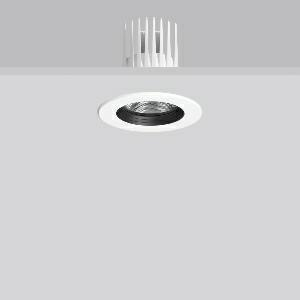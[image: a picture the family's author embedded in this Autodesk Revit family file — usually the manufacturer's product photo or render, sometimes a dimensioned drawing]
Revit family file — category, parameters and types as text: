
# Revit family: heledon_mini_e_901750_002_3_76_2cef
name_source: partatom
category: Lighting Fixtures
units: mm (PartAtom-declared; Revit-internal decimal feet)

## family parameters
Cut with Voids When Loaded = No
Host = Face
Light Source = No
Part Type = Normal
Room Calculation Point = No
Round Connector Dimension = Use Diameter
Shared = No

## types (1)
- HELEDON mini E (1 x LED Modul 935, 3800 lm, 3500)
    Apparent Load = 29 VA
    Approval mark = CE
    CIE Flux Codes = 95 99 100 100 100
    Color Rendering = 92
    Color Temperature = 3500
    Default Elevation = 1800 mm
    Description = Series: HELEDON mini
Round recessed downlight. Housing: die-cast aluminium, powder-coated. Black plastic ring and recessed LED to prevent glare from the side. Optical assembly with reflector made of MIRO-Silver with 98% total light reflection for outstanding efficiency - can be changed without tools. Best colour rendering index Ra>90. Suitable for Recessed ceiling mounting. Installation without tools thanks to spring fastening system. Including separate LED converter with connecting cable 600 mm.High quality converter without flickering and stroboscopic effect. Through-wiring box (5 pole) available as accessory. The following accessories can be mounted without use of tools: interchangeable lenses, decorative glasses, honeycomb louvre, clear and frosted diffusers, white interchangeable plastic ring. 
Colour: traffic white, matt (RAL 9016)
Diameter: 124 mm
Height: 3 mm
Cut-out diameter: 114 mm
Recess height: 170 mm
Luminaire: recess height: 120 mm
Lamp: LED
Socket: without socket
Colour temperature: 3500K
Colour rendering index (CRI): 92
System power: 29 W
Rated luminous flux: 3800 lm
Luminous efficiency: 131 lm/W
Control gear: Converter, dimmable, DALI
Protection class: II
Type of protection: IP 20
    Height = 0 mm  [stored 0 ft]
    Lamp = 1 x LED Modul 935
    Lamp Light Flux = 3800 lm
    Lamp count = 1
    Length = 124 mm  [stored 0.406824 ft]
    Lifetime = 50000 h
    Luminous efficacy = 131 lm/W
    Manufacturer = RZB
    ModVariant = No
    Model = 901750.002.3.76
    Mounting Place = Ceiling
    Mounting Type = Recessed
    Number of Poles = 1
    OnlyDefault = Yes
    Power Factor = 1
    Product Name = HELEDON mini E
    Product group = Recessed downlights
    ProductGroupID = 402
    Protection Class = Protection class II
    Protection Degree = IP 20
    RLX_Detail_Level = 1
    RLX_Emergency_Light_Flux = 0 lm
    RLX_Emergency_Type = 0
    RLX_Emergency_Type_DB = No
    RlxData = <blob elided: 124761 chars, md5=7df65fa0>
    Socket = socket
    Standby Power = 0 W
    System Light Flux = 3800 lm
    System Power = 29 W
    Type Comments = Product without accessories
    Type Image = 901657.002.jpg
    URL = http://relux.com
    VarID = ---
    Voltage = 230 V
    Voltage Range = 220-240 V
    Weight = 0.00 kg
    Width = 0 mm  [stored 0 ft]

note: [stored X ft] marks values corroborated as IEEE doubles in the binary element streams (Revit-internal decimal feet)

## geometry (parser evidence)
native form markers: Blend x4, Sweep x11
no freeform markers — native parametric forms only
